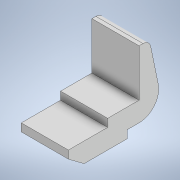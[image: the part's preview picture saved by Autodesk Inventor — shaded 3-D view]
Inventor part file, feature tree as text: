
AUTODESK INVENTOR PART (.ipt)
format: ipt  version: 2022.2 (Build 262287030, 287C)  size: 116,224 bytes
history: native  units: in
note: dims shown in document units (in); Inventor stores cm internally (conversion verified against a paired STEP export)
features: extrude x1, sketch x1
ambient origin geometry x8: Origin, YZ Plane, XZ Plane, XY Plane, X Axis, Y Axis, Z Axis, Center Point
bodies: Solid1 (feature_tree)
feature tree (2):
  extrude  "Extrusion1"  Depth=3.0in
  sketch  "Sketch1"  dims[d0=4.75in d1=2.75in d2=1.25in d3=1.25in d4=0.5in d5=0.25in d6=3.0in d7=0.5in d8=0.5in d9=4.5in d10=2.0in d11=0.75in d12=0.0in d13=3.0in d14=0.0in]
